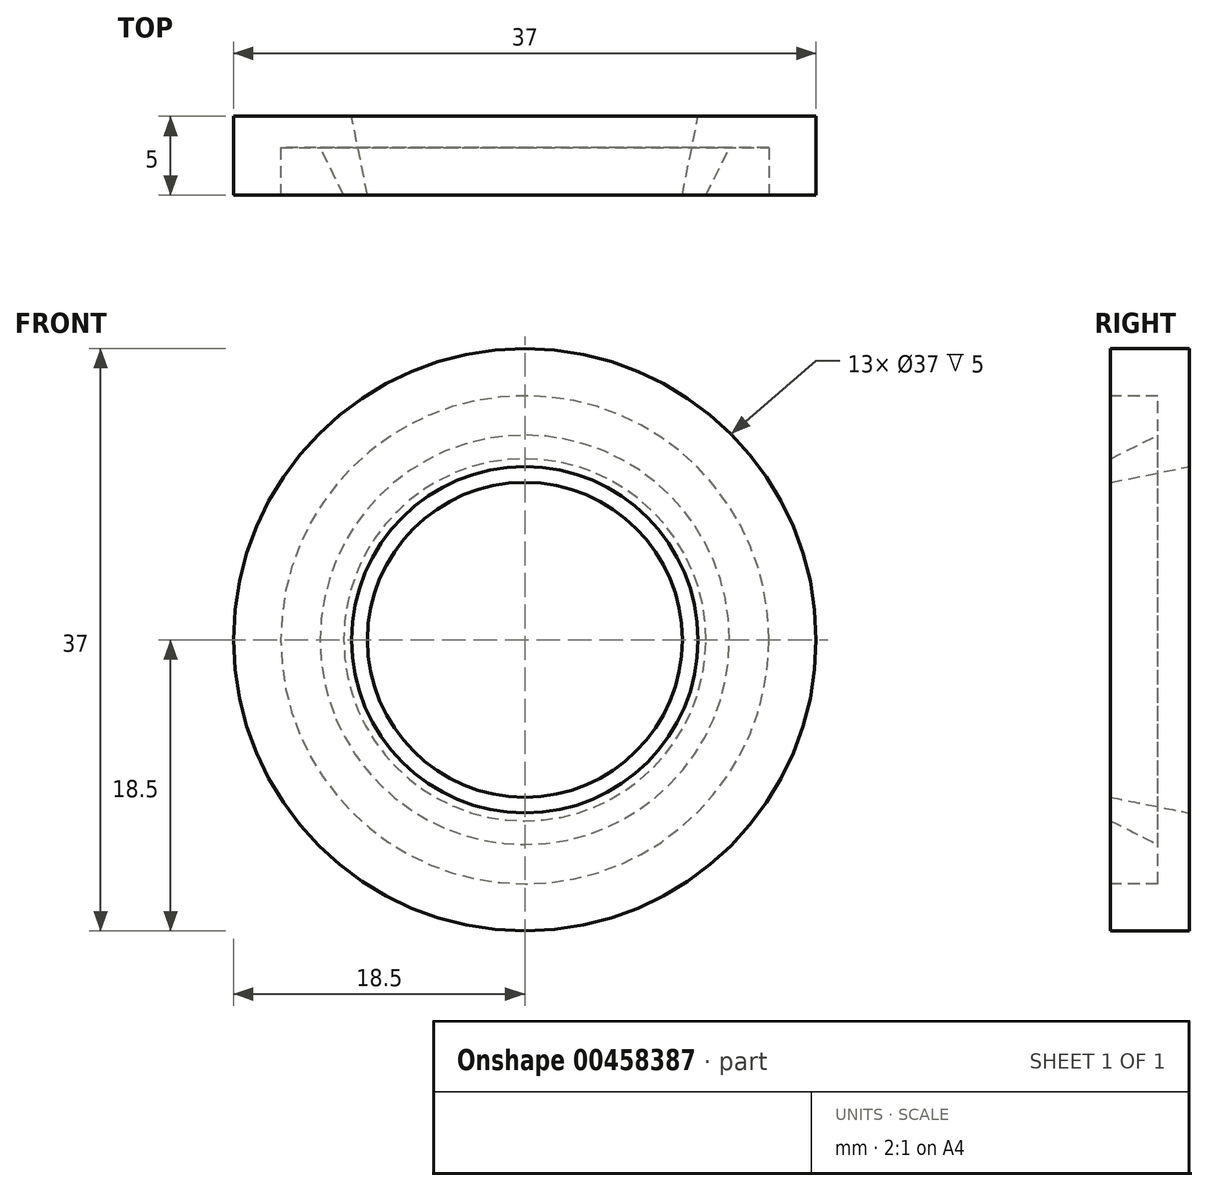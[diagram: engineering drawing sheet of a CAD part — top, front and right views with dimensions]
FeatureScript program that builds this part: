
annotation { "Feature Type Name" : "Feature", "Feature Type Description" : "" }
export const myFeature = defineFeature(function(context is Context, id is Id, definition is map)
    precondition{}
    {
        {
            var Q0;
            Q0=qCreatedBy(makeId("Right.planeOp"),FACE);
            var sketch = newSketch(context, id + "F0", { "sketchPlane" : qUnion([Q0])});
            skLineSegment(sketch, "E0", {"start": v(0, 0) * mm, "end": v(-29.28, 0) * mm, "construction": true});
            skPoint(sketch, "E1", {"position": v(0, 11) * mm});
            skLineSegment(sketch, "E2", {"start": v(0, 11) * mm, "end": v(0, 18.5) * mm});
            skLineSegment(sketch, "E3", {"start": v(0, 18.5) * mm, "end": v(-5, 18.5) * mm});
            skLineSegment(sketch, "E4", {"start": v(-5, 18.5) * mm, "end": v(-5, 15.5) * mm});
            skLineSegment(sketch, "E5", {"start": v(-5, 15.5) * mm, "end": v(-2, 15.5) * mm});
            skLineSegment(sketch, "E6", {"start": v(-2, 15.5) * mm, "end": v(-2, 13) * mm});
            skLineSegment(sketch, "E7", {"start": v(-5, 10) * mm, "end": v(-5, 11.5) * mm});
            skLineSegment(sketch, "E8", {"start": v(-5, 10) * mm, "end": v(0, 11) * mm});
            skLineSegment(sketch, "E9", {"start": v(-5, 11.5) * mm, "end": v(-2, 13) * mm});
            skPoint(sketch, "E10.start.orphan", {"position": v(-5, 0) * mm});
            skSolve(sketch);
        }
        {
            var Q0;
            Q0=sQuery(id+"F0.wireOp",EDGE,"E6");
            var Q1;
            Q1=sQuery(id+"F0.wireOp",EDGE,"E2");
            var Q2;
            Q2=sQuery(id+"F0.wireOp",EDGE,"E8");
            var Q3;
            Q3=sQuery(id+"F0.wireOp",EDGE,"E9");
            var Q4;
            Q4=sQuery(id+"F0.wireOp",EDGE,"E5");
            var Q5;
            Q5=sQuery(id+"F0.wireOp",EDGE,"E4");
            var Q6;
            Q6=sQuery(id+"F0.wireOp",EDGE,"E3");
            var Q7;
            Q7=sQuery(id+"F0.wireOp",EDGE,"E7");
            var Q8;
            Q8=sQuery(id+"F0.wireOp",EDGE,"E0");
            revolve(context, id + "F1", {"bodyType" : ToolBodyType.SURFACE, "surfaceEntities" : qUnion([Q0, Q1, Q2, Q3, Q4, Q5, Q6, Q7]), "axis" : qUnion([Q8]), "revolveType" : RevolveType.FULL});
        }
    });
